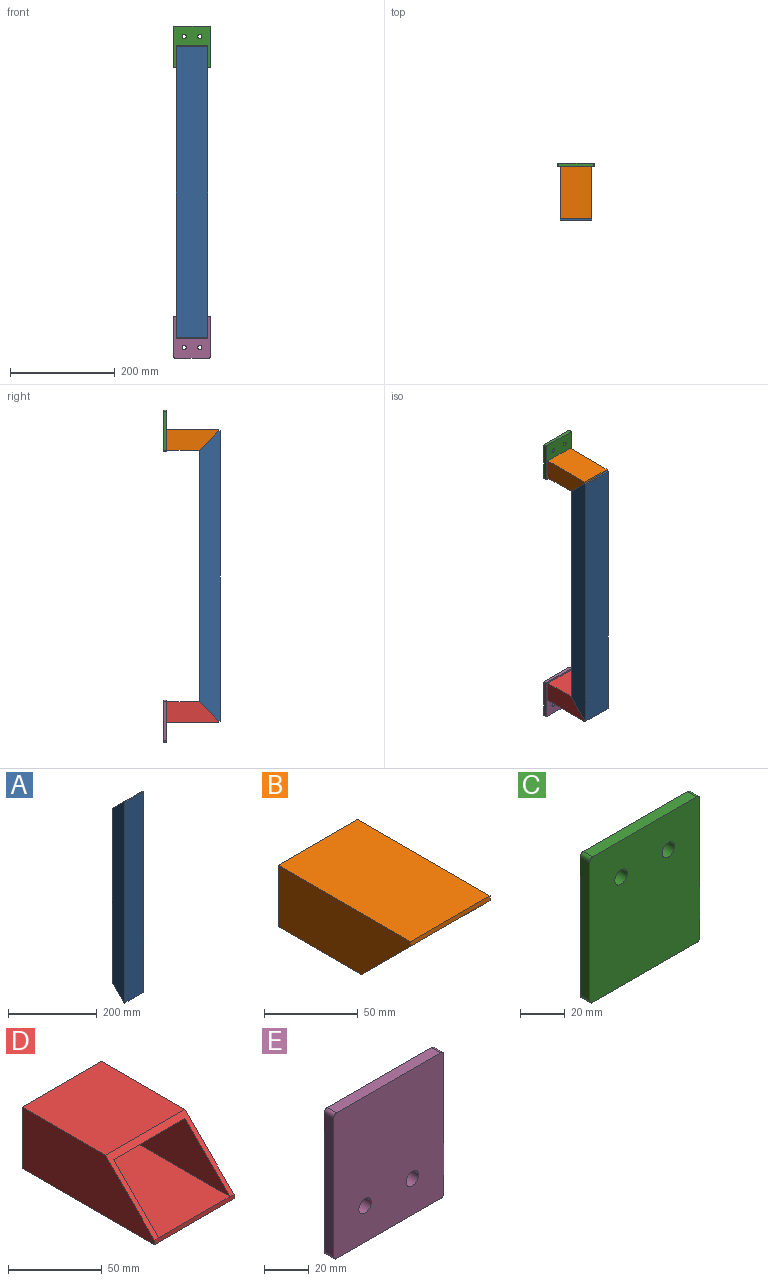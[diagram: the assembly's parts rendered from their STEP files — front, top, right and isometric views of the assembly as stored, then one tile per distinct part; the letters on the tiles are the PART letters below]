
ASSEMBLY  parts=5 mates=4
PART A: 12 faces, bbox 60x40x555 mm
  f0: plane 555x40mm, normal (1,0,0), area 20831mm2, adj f1,f7,f8,f9,f10,f11
  f1: plane 481x60mm, normal (0,1,0), area 28860mm2, adj f0,f2,f10,f11
  f2: plane 555x40mm, normal (-1,0,0), area 20831mm2, adj f1,f7,f8,f9,f10,f11
  f3: plane 555x34mm, normal (-1,0,0), area 17714mm2, adj f5,f6,f10,f11
  f4: plane 555x34mm, normal (1,0,0), area 17714mm2, adj f5,f6,f10,f11
  f5: plane 487x54mm, normal (0,-1,0), area 26298mm2, adj f3,f4,f10,f11
  f6: plane 555x54mm, normal (0,1,0), area 29970mm2, adj f3,f4,f8,f9
  f7: plane 555x60mm, normal (0,-1,0), area 33300mm2, adj f0,f2,f8,f9
  f8: plane 60x3mm, normal (0,0,1), area 180mm2, adj f0,f2,f6,f7,f11
  f9: plane 60x3mm, normal (0,0,-1), area 180mm2, adj f0,f2,f6,f7,f10
  f10: plane 60x37mm, normal (0,0.71,-0.71), area 543.1mm2, adj f0,f1,f2,f3,f4,f5,f9
  f11: plane 60x37mm, normal (0,0.71,0.71), area 543.1mm2, adj f0,f1,f2,f3,f4,f5,f8
PART B: 11 faces, bbox 60x100x40 mm
  f0: plane 66x54mm, normal (0,0,1), area 3564mm2, adj f1,f2,f4,f10
  f1: plane 100x34mm, normal (-1,0,0), area 2822mm2, adj f0,f4,f9,f10
  f2: plane 100x34mm, normal (1,0,0), area 2822mm2, adj f0,f4,f9,f10
  f3: plane 60x3mm, normal (0,-1,0), area 180mm2, adj f5,f6,f7,f9,f10
  f4: plane 60x40mm, normal (0,1,0), area 564mm2, adj f0,f1,f2,f5,f6,f7,f8,f9
  f5: plane 100x40mm, normal (1,0,0), area 3315.5mm2, adj f3,f4,f7,f8,f10
  f6: plane 100x40mm, normal (-1,0,0), area 3315.5mm2, adj f3,f4,f7,f8,f10
  f7: plane 100x60mm, normal (0,0,1), area 6000mm2, adj f3,f4,f5,f6
  f8: plane 63x60mm, normal (0,0,-1), area 3780mm2, adj f4,f5,f6,f10
  f9: plane 100x54mm, normal (0,0,-1), area 5400mm2, adj f1,f2,f3,f4
  f10: plane 60x37mm, normal (0,-0.71,-0.71), area 543.1mm2, adj f0,f1,f2,f3,f5,f6,f8
PART C: 12 faces, bbox 70x6x80 mm
  f0: plane 66x6mm, normal (0,0,-1), area 396mm2, adj f1,f9,f10,f11
  f1: cylinder r=2mm len=6mm, axis (0,1,0), area 18.8mm2, adj f0,f2,f10,f11
  f2: plane 76x6mm, normal (1,0,0), area 456mm2, adj f1,f3,f10,f11
  f3: cylinder r=2mm len=6mm, axis (0,1,0), area 18.8mm2, adj f2,f4,f10,f11
  f4: plane 66x6mm, normal (0,0,1), area 396mm2, adj f3,f5,f10,f11
  f5: cylinder r=2mm len=6mm, axis (0,1,0), area 18.8mm2, adj f4,f6,f10,f11
  f6: plane 76x6mm, normal (-1,0,0), area 456mm2, adj f5,f9,f10,f11
  f7: cylinder r=4mm len=8mm, axis (0,1,0), area 150.8mm2, adj f10,f11
  f8: cylinder r=4mm len=8mm, axis (0,1,0), area 150.8mm2, adj f10,f11
  f9: cylinder r=2mm len=6mm, axis (0,1,0), area 18.8mm2, adj f0,f6,f10,f11
  f10: plane 80x70mm, normal (0,-1,0), area 5496mm2, adj f0,f1,f2,f3,f4,f5,f6,f7
  f11: plane 80x70mm, normal (0,1,0), area 5496mm2, adj f0,f1,f2,f3,f4,f5,f6,f7
PART D: 11 faces, bbox 60x100x40 mm
  f0: plane 100x40mm, normal (1,0,0), area 3315.5mm2, adj f2,f6,f7,f8,f10
  f1: plane 100x40mm, normal (-1,0,0), area 3315.5mm2, adj f2,f6,f7,f8,f10
  f2: plane 63x60mm, normal (0,0,1), area 3780mm2, adj f0,f1,f7,f10
  f3: plane 100x34mm, normal (-1,0,0), area 2822mm2, adj f4,f7,f9,f10
  f4: plane 66x54mm, normal (0,0,-1), area 3564mm2, adj f3,f5,f7,f10
  f5: plane 100x34mm, normal (1,0,0), area 2822mm2, adj f4,f7,f9,f10
  f6: plane 60x3mm, normal (0,-1,0), area 180mm2, adj f0,f1,f8,f9,f10
  f7: plane 60x40mm, normal (0,1,0), area 564mm2, adj f0,f1,f2,f3,f4,f5,f8,f9
  f8: plane 100x60mm, normal (0,0,-1), area 6000mm2, adj f0,f1,f6,f7
  f9: plane 100x54mm, normal (0,0,1), area 5400mm2, adj f3,f5,f6,f7
  f10: plane 60x37mm, normal (0,-0.71,0.71), area 543.1mm2, adj f0,f1,f2,f3,f4,f5,f6
PART E: 12 faces, bbox 70x6x80 mm
  f0: plane 66x6mm, normal (0,0,-1), area 396mm2, adj f1,f9,f10,f11
  f1: cylinder r=2mm len=6mm, axis (0,1,0), area 18.8mm2, adj f0,f2,f10,f11
  f2: plane 76x6mm, normal (1,0,0), area 456mm2, adj f1,f3,f10,f11
  f3: cylinder r=2mm len=6mm, axis (0,1,0), area 18.8mm2, adj f2,f4,f10,f11
  f4: plane 66x6mm, normal (0,0,1), area 396mm2, adj f3,f5,f10,f11
  f5: cylinder r=2mm len=6mm, axis (0,1,0), area 18.8mm2, adj f4,f6,f10,f11
  f6: plane 76x6mm, normal (-1,0,0), area 456mm2, adj f5,f9,f10,f11
  f7: cylinder r=4mm len=8mm, axis (0,1,0), area 150.8mm2, adj f10,f11
  f8: cylinder r=4mm len=8mm, axis (0,1,0), area 150.8mm2, adj f10,f11
  f9: cylinder r=2mm len=6mm, axis (0,1,0), area 18.8mm2, adj f0,f6,f10,f11
  f10: plane 80x70mm, normal (0,-1,0), area 5496mm2, adj f0,f1,f2,f3,f4,f5,f6,f7
  f11: plane 80x70mm, normal (0,1,0), area 5496mm2, adj f0,f1,f2,f3,f4,f5,f6,f7
PLACE A t=(-164.76,45.51,-66.54)mm
PLACE B t=(-164.76,78.51,451.46)mm
PLACE C t=(-164.76,134.51,488.53)mm
PLACE D t=(-164.76,78.51,-69.54)mm
PLACE E t=(-164.76,134.51,-66.61)mm
MATE planar B.f10 <-> A.f11  axis (0,-0.71,-0.71) through (-164.76,65.51,451.46)mm
MATE planar D.f10 <-> A.f10  axis (0,-0.71,0.71) through (-164.76,65.51,-29.54)mm
MATE planar E.f10 <-> D.f7  axis (0,-1,0) through (-164.76,128.51,-26.61)mm
MATE planar C.f10 <-> B.f4  axis (0,-1,0) through (-164.76,128.51,448.53)mm
